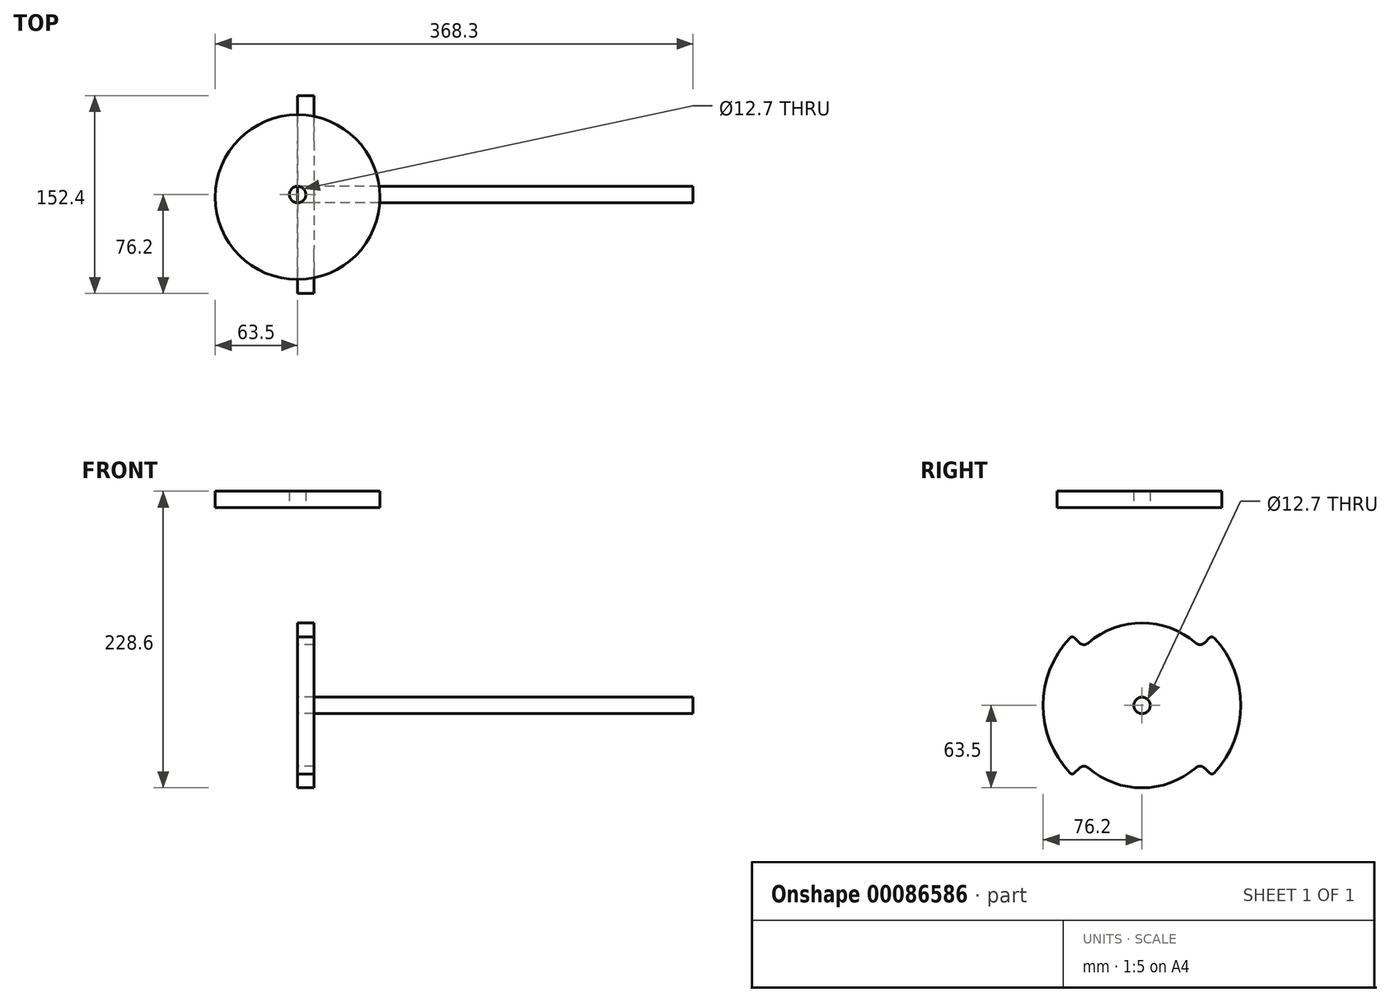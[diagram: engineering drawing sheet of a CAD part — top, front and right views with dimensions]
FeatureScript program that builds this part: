
annotation { "Feature Type Name" : "Feature", "Feature Type Description" : "" }
export const myFeature = defineFeature(function(context is Context, id is Id, definition is map)
    precondition{}
    {
        {
            var Q0;
            Q0=qCreatedBy(makeId("Right.planeOp"),FACE);
            var sketch = newSketch(context, id + "F0", { "sketchPlane" : qUnion([Q0])});
            skCircle(sketch, "E0", {"center": v(0, 0) * mm, "radius": 76.2 * mm});
            skLineSegment(sketch, "E1", {"start": v(-53.88, 53.88) * mm, "end": v(53.88, -53.88) * mm, "construction": true});
            skLineSegment(sketch, "E2", {"start": v(0, -76.2) * mm, "end": v(0, 76.2) * mm, "construction": true});
            skLineSegment(sketch, "E3.MirrorCS", {"start": v(53.88, 53.88) * mm, "end": v(-53.88, -53.88) * mm, "construction": true});
            skLineSegment(sketch, "E4", {"start": v(53.88, 53.88) * mm, "end": v(44.9, 44.9) * mm});
            skLineSegment(sketch, "E5", {"start": v(-53.88, 53.88) * mm, "end": v(-44.9, 44.9) * mm});
            skArc(sketch, "E6", {"start": v(-44.9, 44.9) * mm, "mid": v(0, 63.5) * mm, "end": v(44.9, 44.9) * mm});
            skLineSegment(sketch, "E7", {"start": v(-76.2, 0) * mm, "end": v(76.2, 0) * mm, "construction": true});
            skLineSegment(sketch, "E8.MirrorCS", {"start": v(-53.88, -53.88) * mm, "end": v(-44.9, -44.9) * mm});
            skArc(sketch, "E9.MirrorCS", {"start": v(-44.9, -44.9) * mm, "mid": v(0, -63.5) * mm, "end": v(44.9, -44.9) * mm});
            skLineSegment(sketch, "E10.MirrorCS", {"start": v(53.88, -53.88) * mm, "end": v(44.9, -44.9) * mm});
            skCircle(sketch, "E11", {"center": v(0, 0) * mm, "radius": 6.35 * mm});
            skSolve(sketch);
        }
        {
            var Q0;
            {var subQ1=sQuery(id+"F0.wireOp",EDGE,"E4");Q0=makeQuery(id+"F0.imprint","IMPRINT",FACE,{"disambiguationData":[TD([[makeQuery(id+"F0.imprint","IMPRINT",EDGE,{"derivedFrom":subQ1}),1.0]])]});}
            extrude(context, id + "F1", {"entities" : qUnion([Q0]), "depth" : 12.7 * mm});
        }
        {
            var Q0;
            Q0=makeQuery(id+"F1.opExtrude","SWEPT_EDGE",EDGE,{"disambiguationData":[OSD([sQuery(id+"F0.wireOp",EDGE,"E0"),sQuery(id+"F0.wireOp",EDGE,"E5")])]});
            var Q1;
            Q1=makeQuery(id+"F1.opExtrude","SWEPT_EDGE",EDGE,{"disambiguationData":[OSD([sQuery(id+"F0.wireOp",EDGE,"E0"),sQuery(id+"F0.wireOp",EDGE,"E4")])]});
            var Q2;
            Q2=makeQuery(id+"F1.opExtrude","SWEPT_EDGE",EDGE,{"disambiguationData":[OSD([sQuery(id+"F0.wireOp",EDGE,"E0"),sQuery(id+"F0.wireOp",EDGE,"E8.MirrorCS")])]});
            var Q3;
            Q3=makeQuery(id+"F1.opExtrude","SWEPT_EDGE",EDGE,{"disambiguationData":[OSD([sQuery(id+"F0.wireOp",EDGE,"E0"),sQuery(id+"F0.wireOp",EDGE,"E10.MirrorCS")])]});
            fillet(context, id + "F2", {"entities" : qUnion([Q0, Q1, Q2, Q3]), "radius" : 2.54 * mm, "tangentPropagation" : true, "allowEdgeOverflow" : false});
        }
        {
            var Q0;
            Q0=makeQuery(id+"F1.opExtrude","SWEPT_EDGE",EDGE,{"disambiguationData":[OSD([sQuery(id+"F0.wireOp",EDGE,"E8.MirrorCS"),sQuery(id+"F0.wireOp",EDGE,"E9.MirrorCS")])]});
            var Q1;
            Q1=makeQuery(id+"F1.opExtrude","SWEPT_EDGE",EDGE,{"disambiguationData":[OSD([sQuery(id+"F0.wireOp",EDGE,"E9.MirrorCS"),sQuery(id+"F0.wireOp",EDGE,"E10.MirrorCS")])]});
            var Q2;
            Q2=makeQuery(id+"F1.opExtrude","SWEPT_EDGE",EDGE,{"disambiguationData":[OSD([sQuery(id+"F0.wireOp",EDGE,"E4"),sQuery(id+"F0.wireOp",EDGE,"E6")])]});
            var Q3;
            Q3=makeQuery(id+"F1.opExtrude","SWEPT_EDGE",EDGE,{"disambiguationData":[OSD([sQuery(id+"F0.wireOp",EDGE,"E5"),sQuery(id+"F0.wireOp",EDGE,"E6")])]});
            fillet(context, id + "F3", {"entities" : qUnion([Q0, Q1, Q2, Q3]), "radius" : 5.08 * mm, "tangentPropagation" : true, "allowEdgeOverflow" : false});
        }
        {
            var Q0;
            Q0=qCreatedBy(makeId("Top.planeOp"),FACE);
            cPlane(context, id + "F4", {"entities" : qUnion([Q0]), "cplaneType" : CPlaneType.OFFSET, "offset" : 152.4 * mm, "width" : 152.4 * mm, "height" : 152.4 * mm});
        }
        {
            var Q0;
            Q0=makeQuery(id+"F0.imprint","IMPRINT",FACE,{"disambiguationData":[TD([[makeQuery(id+"F0.imprint","IMPRINT",EDGE,{"derivedFrom":sQuery(id+"F0.wireOp",EDGE,"E11")}),1.0]])]});
            extrude(context, id + "F5", {"entities" : qUnion([Q0]), "depth" : 304.8 * mm});
        }
        {
            var Q0;
            Q0=qCreatedBy(id+"F4.planeOp",FACE);
            var sketch = newSketch(context, id + "F6", { "sketchPlane" : qUnion([Q0])});
            skCircle(sketch, "E12", {"center": v(0, -2) * mm, "radius": 63.5 * mm});
            skCircle(sketch, "E13", {"center": v(0, 0) * mm, "radius": 6.35 * mm});
            skSolve(sketch);
        }
        {
            var Q0;
            Q0=makeQuery(id+"F6.imprint","IMPRINT",FACE,{"disambiguationData":[TD([[makeQuery(id+"F6.imprint","IMPRINT",EDGE,{"derivedFrom":sQuery(id+"F6.wireOp",EDGE,"E12")}),1.0]])]});
            extrude(context, id + "F7", {"entities" : qUnion([Q0]), "depth" : 12.7 * mm});
        }
    });
